# Revit family: 62_HD_Series
name_source: partatom
category: Mechanical Equipment
revit_build: Autodesk Revit 2013 (Build: 20120221_2030(x64)
units: mm (PartAtom-declared; Revit-internal decimal feet)

## types (43) — shared parameters
Assembly Code = D2010900
Default Elevation = 0"
Description = Commercial Effluent Pumps
Dry Pit (5-15 BHP) = Yes
Flange = ANSI B16.1
Height = 33 5/8"
Hertz = 60
High Temperature (5-10 BHP) = Yes
Impeller Type = Ductile Iron Semi-Open
Impeller Type (Optional) Bronze Semi-open = No
Impeller Type (Optional) Ductile Iron Vortex = No
Installation Type = Floor Mounted
Insulation = Class F
Inverter Duty Submersible (5-15 BHP Only) = No
Length = 18 3/8"
Manufacturer = Zoeller
Masterformat Number = 33 36 16
Masterformat Title = Utility Septic Tank Effluent Pumps
Material = Cast Iron-Zoeller-Powder Coated Epoxy
Max. Stator Temp. = 311 °F
Max. Water Temp. = 104 °F
Min. Recommended Fluid Level = 24"
Model = 6220-4"
Moisture Sensor (Optional) = Moisture Sensing Probes (Requires a circuit in control panel)
Motor Design Letter = NEMA B
Motor Shaft = 416 S.S.
Motor Thermal Shutoff (Single Phase Only) = Thermal Sensors With Automatic Reset
Motor Type = Standard Submersible
O-Rings (Optional) Viton = No
O-Rings and Cover Gasket = Buna-N
Omniclass Table 23 Code = 23.60.30.21
Omniclass Table 23 Title = Pumps
Operation = Non-Automatic
Power Cord = <20 = #12-4 SO (Models with a FLA greater than 36.7 amps use #8-4 gauge power cord; #4-4 for less than 36.7)
Price = Prices may vary. Please consult Manufacturer Representative for most up-to-date price list.
Product Page URL = http://www.zoellerengprod.com
RPM = 1750
Sensor Cord Size = #18-5
Shaft Seal Lower (Options) = Carbon/Silicon Carbide, Silicon Carbide/Silicon Carbide
Shaft Seal Upper (Options) = Silicon Carbide/Carbon, Silicon Carbide/Silicon Carbide
Shaft Seal Upper Standard = Carbon/Ceramic
Shipping Weight = 350lbs(159kg)
Solid Size = 3" (75 mm)
Tandem Seals = Standard
Type SOW Power Cord Length = 300"
URL = http://www.zoellerengprod.com
Warranty Information = 36 Months (Limited)
Waste Connection = Yes
Width = 14 11/16"

## per-type parameters (varying)
| type | Apparent Load | Connecter Description | Discharge Diameter | Discharge Radius | Flow 6220 @ 5', 6221-6224 @ 10' | Full Load Amps | Impeller Diameter | Locked Rotor Amps (Voltage Dependant) | Maximum KW Input | Motor | NEC Locked Rotor Code | Phase | Service Factor | Type | Void Visibility | Void Visibility 2 | Voltage |
| 6220-4" 230V 1Ph | 6325 VA | 4" Horizontal Discharge | 4" | 2" | 785 GPM | 28 A | 6 7/8" | 91.0 | 5.2 | 5.0 BHP | D | 1 | 1.2 | Permanent Split Capacitor | -15" | 0" | 230 V |
| 6220-4" 200V 3Ph | 3500 VA | 4" Horizontal Discharge | 4" | 2" | 785 GPM | 18 A | 6 7/8" | 61.9 | 5.2 | 5.0 BHP | D | 3 | 1.2 | 3Phase | -15" | 0" | 200 V |
| 6220-4" 230V 3Ph | 3496 VA | 4" Horizontal Discharge | 4" | 2" | 785 GPM | 15 A | 6 7/8" | 53.8 | 5.2 | 5.0 BHP | D | 3 | 1.2 | 3Phase | -15" | 0" | 230 V |
| 6220-4" 460V 3Ph | 3496 VA | 4" Horizontal Discharge | 4" | 2" | 785 GPM | 8 A | 6 7/8" | 26.9 | 5.2 | 5.0 BHP | D | 3 | 1.2 | 3Phase | -15" | 0" | 460 V |
| 6220-4" 575V 3Ph | 3508 VA | 4" Horizontal Discharge | 4" | 2" | 785 GPM | 6 A | 6 7/8" | 21.8 | 5.2 | 5.0 BHP | D | 3 | 1.2 | 3Phase | -15" | 0" | 575 V |
| 6220-6" 230V 1Ph | 6325 VA | 6" Horizontal Discharge | 6" | 3" | 785 GPM | 28 A | 6 7/8" | 91.0 | 5.2 | 5.0 BHP | D | 1 | 1.2 | Permanent Split Capacitor | -9 27/32" | 12" | 230 V |
| 6220-6" 200V 3Ph | 3500 VA | 6" Horizontal Discharge | 6" | 3" | 785 GPM | 18 A | 6 7/8" | 61.9 | 5.2 | 5.0 BHP | D | 3 | 1.2 | 3 Phase | -9 27/32" | 12" | 200 V |
| 6220-6" 460V 3Ph | 3496 VA | 6" Horizontal Discharge | 6" | 3" | 785 GPM | 8 A | 6 7/8" | 26.9 | 5.2 | 5.0 BHP | D | 3 | 1.2 | 3 Phase | -9 27/32" | 12" | 460 V |
| 6220-6" 575V 3Ph | 3508 VA | 6" Horizontal Discharge | 6" | 3" | 785 GPM | 6 A | 6 7/8" | 21.8 | 5.2 | 5.0 BHP | D | 3 | 1.2 | 3 Phase | -9 27/32" | 12" | 575 V |
| 6221-4" 230V 1Ph | 8441 VA | 4" Horizontal Discharge | 4" | 2" | 860 GPM | 37 A | 7 3/8" | 137.0 | 7.8 | 7.5 BHP | F | 1 | 1.2 | Permanent Split Capacitor | -15" | 0" | 230 V |
| 6221-4" 200V 3Ph | 5000 VA | 4" Horizontal Discharge | 4" | 2" | 860 GPM | 25 A | 7 3/8" | 109.0 | 7.8 | 7.5 BHP | F | 3 | 1.2 | 3 Phase | -15" | 0" | 200 V |
| 6221-4" 230V 3Ph | 5060 VA | 4" Horizontal Discharge | 4" | 2" | 860 GPM | 22 A | 7 3/8" | 95.0 | 7.8 | 7.5 BHP | F | 3 | 1.2 | 3 Phase | -15" | 0" | 230 V |
| 6221-4" 460V 3Ph | 5060 VA | 4" Horizontal Discharge | 4" | 2" | 860 GPM | 11 A | 7 3/8" | 47.5 | 7.8 | 7.5 BHP | F | 3 | 1.2 | 3 Phase | -15" | 0" | 460 V |
| 6221-4" 575V 3Ph | 5175 VA | 4" Horizontal Discharge | 4" | 2" | 860 GPM | 9 A | 7 3/8" | 37.8 | 7.8 | 7.5 BHP | F | 3 | 1.2 | 3 Phase | -15" | 0" | 575 V |
| 6221-6" 230V 1Ph | 8441 VA | 6" Horizontal Discharge | 6" | 3" | 860 GPM | 37 A | 7 3/8" | 137.0 | 7.8 | 7.5 BHP | F | 1 | 1.2 | Permanent Split Capacitor | -9 27/32" | 12" | 230 V |
| 6221-6" 200V 3Ph | 5000 VA | 6" Horizontal Discharge | 6" | 3" | 860 GPM | 25 A | 7 3/8" | 109.0 | 7.8 | 7.5 BHP | F | 3 | 1.2 | 3 Phase | -9 27/32" | 12" | 200 V |
| 6221-6" 230V 3Ph | 5060 VA | 6" Horizontal Discharge | 6" | 3" | 860 GPM | 22 A | 7 3/8" | 95.0 | 7.8 | 7.5 BHP | F | 3 | 1.2 | 3 Phase | -9 27/32" | 12" | 230 V |
| 6221-6" 460V 3Ph | 5060 VA | 6" Horizontal Discharge | 6" | 3" | 860 GPM | 11 A | 7 3/8" | 47.5 | 7.8 | 7.5 BHP | F | 3 | 1.2 | 3 Phase | -9 27/32" | 12" | 460 V |
| 6221-6" 575V 3Ph | 5175 VA | 6" Horizontal Discharge | 6" | 3" | 860 GPM | 9 A | 7 3/8" | 37.8 | 7.8 | 7.5 BHP | F | 3 | 1.2 | 3 Phase | -9 27/32" | 12" | 575 V |
| 6222-4" 200V 3Ph | 6400 VA | 4" Horizontal Discharge | 4" | 2" | 957 GPM | 32 A | 7 3/4" | 109.0 | 9.8 | 10.0 BHP | C | 3 | 1.2 | 3 Phase | -15" | 0" | 200 V |
| 6222-4" 230V 3Ph | 6440 VA | 4" Horizontal Discharge | 4" | 2" | 957 GPM | 28 A | 7 3/4" | 95.0 | 9.8 | 10.0 BHP | C | 3 | 1.2 | 3 Phase | -15" | 0" | 230 V |
| 6222-4" 460V 3Ph | 6440 VA | 4" Horizontal Discharge | 4" | 2" | 957 GPM | 14 A | 7 3/4" | 47.5 | 9.8 | 10.0 BHP | C | 3 | 1.2 | 3 Phase | -15" | 0" | 460 V |
| 6222-4" 575V 3Ph | 6325 VA | 4" Horizontal Discharge | 4" | 2" | 957 GPM | 11 A | 7 3/4" | 37.8 | 9.8 | 10.0 BHP | C | 3 | 1.2 | 3 Phase | -15" | 0" | 575 V |
| 6222-6" 200V 3Ph | 3488 VA | 6" Horizontal Discharge | 6" | 3" | 957 GPM | 32 A | 7 3/4" | 109 | 9.8 | 10.0 BHP | C | 3 | 1.2 | 3 Phase | -9 27/32" | 12" | 200 V |
| 6222-6" 230V 3Ph | 6440 VA | 6" Horizontal Discharge | 6" | 3" | 957 GPM | 28 A | 7 3/4" | 95.0 | 9.8 | 10.0 BHP | C | 3 | 1.2 | 3 Phase | -9 27/32" | 12" | 230 V |
| 6222-6" 460V 3Ph | 6440 VA | 6" Horizontal Discharge | 6" | 3" | 957 GPM | 14 A | 7 3/4" | 47.5 | 9.8 | 10.0 BHP | C | 3 | 1.2 | 3 Phase | -9 27/32" | 12" | 460 V |
| 6222-6" 575V 3Ph | 6325 VA | 6" Horizontal Discharge | 6" | 3" | 957 GPM | 11 A | 7 3/4" | 37.8 | 9.8 | 10.0 BHP | C | 3 | 1.2 | 3 Phase | -9 27/32" | 12" | 575 V |
| 6223-4" 200V 3Ph | 9660 VA | 4" Horizontal Discharge | 4" | 2" | 1110 GPM | 48 A | 8 5/8" | 197.0 | 13.5 | 15.0 BHP | E | 3 | 1.2 | 3 Phase | -15" | 0" | 200 V |
| 6223-4" 230V 3Ph | 9591 VA | 4" Horizontal Discharge | 4" | 2" | 1110 GPM | 42 A | 8 5/8" | 172.0 | 13.5 | 15.0 BHP | E | 3 | 1.2 | 3 Phase | -15" | 0" | 230 V |
| 6223-4" 460V 3Ph | 9614 VA | 4" Horizontal Discharge | 4" | 2" | 1110 GPM | 21 A | 8 5/8" | 86.0 | 13.5 | 15.0 BHP | E | 3 | 1.2 | 3 Phase | -15" | 0" | 460 V |
| 6223-4" 575V 3Ph | 9430 VA | 4" Horizontal Discharge | 4" | 2" | 1110 GPM | 16 A | 8 5/8" | 70.0 | 13.5 | 15.0 BHP | E | 3 | 1.2 | 3 Phase | -15" | 0" | 575 V |
| 6223-6" 200V 3Ph | 9660 VA | 6" Horizontal Discharge | 6" | 3" | 1110 GPM | 48 A | 8 5/8" | 197.0 | 13.5 | 15.0 BHP | E | 3 | 1.2 | 3 Phase | -9 27/32" | 12" | 200 V |
| 6223-6" 230V 3Ph | 9591 VA | 6" Horizontal Discharge | 6" | 3" | 1110 GPM | 42 A | 8 5/8" | 172.0 | 13.5 | 15.0 BHP | E | 3 | 1.2 | 3 Phase | -9 27/32" | 12" | 230 V |
| 6223-6" 460V 3Ph | 9614 VA | 6" Horizontal Discharge | 6" | 3" | 1110 GPM | 21 A | 8 5/8" | 86.0 | 13.5 | 15.0 BHP | E | 3 | 1.2 | 3 Phase | -9 27/32" | 12" | 460 V |
| 6223-6" 575V 3Ph | 9430 VA | 6" Horizontal Discharge | 6" | 3" | 1110 GPM | 16 A | 8 5/8" | 70.0 | 13.5 | 15.0 BHP | E | 3 | 1.2 | 3 Phase | -9 27/32" | 12" | 575 V |
| 6224-4" 230V 3Ph | 12420 VA | 4" Horizontal Discharge | 4" | 2" | 1150 GPM | 54 A | 9 1/2" | 172.0 | 16.8 | 20.0 BHP | B | 3 | 1.0 | 3 Phase | -15" | 0" | 230 V |
| 6224-4" 460V 3Ph | 12420 VA | 4" Horizontal Discharge | 4" | 2" | 1150 GPM | 27 A | 9 1/2" | 86.0 | 16.8 | 20.0 BHP | B | 3 | 1.0 | 3 Phase | -15" | 0" | 460 V |
| 6224-4" 575V 3Ph | 12650 VA | 4" Horizontal Discharge | 4" | 2" | 1150 GPM | 22 A | 9 1/2" | 70.0 | 16.8 | 20.0 BHP | B | 3 | 1.0 | 3 Phase | -15" | 0" | 575 V |
| 6224-4" 200V 3Ph | 11880 VA | 4" Horizontal Discharge | 4" | 2" | 1150 GPM | 59 A | 9 1/2" | 197.0 | 16.8 | 20.0 BHP | B | 3 | 1.0 | 3 Phase | -15" | 0" | 200 V |
| 6224-6" 200V 3Ph | 11880 VA | 6" Horizontal Discharge | 6" | 3" | 1150 GPM | 59 A | 9 1/2" | 197.0 | 16.8 | 20.0 BHP | B | 3 | 1.0 | 3 Phase | -9 27/32" | 12" | 200 V |
| 6224-6" 230V 3Ph | 12420 VA | 6" Horizontal Discharge | 6" | 3" | 1150 GPM | 54 A | 9 1/2" | 172.0 | 16.8 | 20.0 BHP | B | 3 | 1.0 | 3 Phase | -9 27/32" | 12" | 230 V |
| 6224-6" 460V 3Ph | 12420 VA | 6" Horizontal Discharge | 6" | 3" | 1150 GPM | 27 A | 9 1/2" | 86.0 | 16.8 | 20.0 BHP | B | 3 | 1.0 | 3 Phase | -9 27/32" | 12" | 460 V |
| 6224-6" 575V 3Ph | 12650 VA | 6" Horizontal Discharge | 6" | 3" | 1150 GPM | 22 A | 9 1/2" | 70.0 | 16.8 | 20.0 BHP | B | 3 | 1.0 | 3 Phase | -9 27/32" | 12" | 575 V |

## geometry (parser evidence)
native form markers: Blend x2, Sweep x1
no freeform markers — native parametric forms only
